# Revit family: STS-411К_RV17_LOD_400
name_source: partatom
category: Электрооборудование
revit_build: Autodesk Revit 2017 (Build: 20170118_1100(x64)
units: mm (PartAtom-declared; Revit-internal decimal feet)

## family parameters
Всегда вертикально = Да
Конфигурация панели = Два столбца, слева направо
На основе рабочей плоскости = Нет
Общий = Нет
При загрузке вырезать с полостями = Нет
Размер круглого соединителя = Использовать диаметр
Тип детали = Щит
Точка расчета площади = Нет

## types (1)
- STS-411K
    ADSK_URL страницы изделия = https://stilsoft.ru
    ADSK_Единица измерения = шт.
    ADSK_Завод-изготовитель = ООО «Основа Безопасности»
    ADSK_Количество = 1
    ADSK_Марка = СТВФ.426469.012
    ADSK_Масса = 2
    ADSK_Наименование = STS-411К
    ADSK_Размер_Высота = 270 мм
    ADSK_Размер_Глубина = 78 мм
    ADSK_Размер_Ширина = 290 мм
    Диапазон рабочих температур, °С = от +5 до +50
    Длина кода ключа (пропуска), символов = 1-8
    Интерфейс считывателей (1) = Wiegand 26
    Интерфейс считывателей (2) = Wiegand 40/42
    Информационная ёмкость (количество ШС) = 16
    Количество поддерживаемых считывающих устройств, не более, шт = 2
    Количество реле, шт = 8
    Контактный набор = 1 перекл.
    Максимальное время работы в автономном режиме, ч = 3.8
    Максимальное количество ключей (пропусков) ОПС, шт. = 16
    Максимальное количество подключаемых извещателей, при суммарном потреблении тока не более 3 мА, шт. = 20
    Максимальное удаление считывающих устройств от контролера, не более, м = 100
    Максимальный коммутируемый ток, А = 12 А
    Максимальный потребляемый контроллером ток от сети переменного тока (без дополнительных внешних потребителей), А = 0 А
    Напряжение = 220
    Напряжение питания в автономном режиме, В = от 10,5 до 14,2
    Номинальное рабочее напряжение, В = 12
    Предельное значение сопротивления проводов ШС, кОм = 0.1
    Стандарт интерфейса связи = 10 Base-T Ethernet (гнездо RJ-45), RS-485
Ethernet
(гнездо RJ-45),
RS-485
    Ток коммутации (постоянный), А = 0 А
